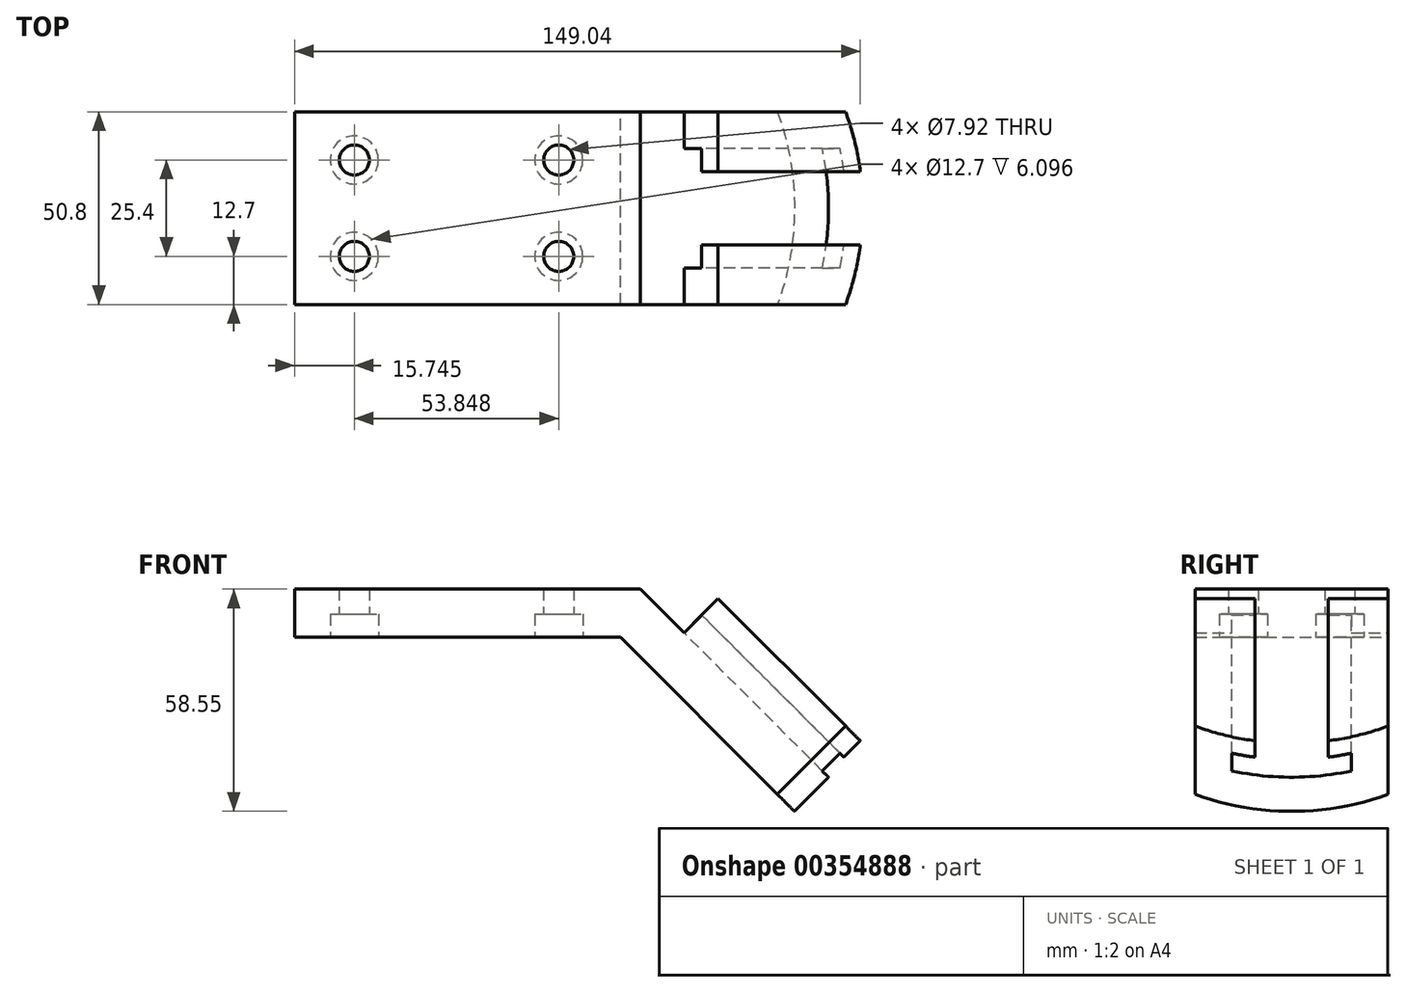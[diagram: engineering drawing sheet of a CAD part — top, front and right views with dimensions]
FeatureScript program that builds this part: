
annotation { "Feature Type Name" : "Feature", "Feature Type Description" : "" }
export const myFeature = defineFeature(function(context is Context, id is Id, definition is map)
    precondition{}
    {
        {
            var Q0;
            Q0=qCreatedBy(makeId("Front.planeOp"),FACE);
            var sketch = newSketch(context, id + "F0", { "sketchPlane" : qUnion([Q0])});
            skLineSegment(sketch, "E0.0.0", {"start": v(-91.11, -12.7) * mm, "end": v(-5.26, -12.7) * mm});
            skLineSegment(sketch, "E0.0.2", {"start": v(0, 0) * mm, "end": v(-91.11, 0) * mm});
            skLineSegment(sketch, "E0.0.3", {"start": v(-91.11, 0) * mm, "end": v(-91.11, -12.7) * mm});
            skLineSegment(sketch, "E1", {"start": v(0, 0) * mm, "end": v(49.57, -49.57) * mm});
            skLineSegment(sketch, "E2", {"start": v(49.57, -49.57) * mm, "end": v(40.6, -58.55) * mm});
            skLineSegment(sketch, "E3", {"start": v(40.6, -58.55) * mm, "end": v(-5.26, -12.7) * mm});
            skLineSegment(sketch, "E4", {"start": v(0, 0) * mm, "end": v(-18.71, 18.71) * mm, "construction": true});
            skLineSegment(sketch, "E5", {"start": v(49.57, -49.57) * mm, "end": v(58.55, -40.6) * mm});
            skLineSegment(sketch, "E6", {"start": v(58.55, -40.6) * mm, "end": v(20.47, -2.51) * mm});
            skLineSegment(sketch, "E7", {"start": v(20.47, -2.51) * mm, "end": v(11.5, -11.5) * mm});
            skSolve(sketch);
        }
        {
            var Q0;
            Q0=makeQuery(id+"F0.imprint","IMPRINT",FACE,{"disambiguationData":[TD([[makeQuery(id+"F0.imprint","IMPRINT",EDGE,{"derivedFrom":sQuery(id+"F0.wireOp",EDGE,"E0.0.0")}),1.0]])]});
            var Q1;
            {var subQ0=sQuery(id+"F0.wireOp",EDGE,"E5");Q1=makeQuery(id+"F0.imprint","IMPRINT",FACE,{"disambiguationData":[TD([[makeQuery(id+"F0.imprint","IMPRINT",EDGE,{"derivedFrom":subQ0}),1.0]])]});}
            extrude(context, id + "F1", {"entities" : qUnion([Q0, Q1]), "depth" : 50.8 * mm, "symmetric" : true});
        }
        {
            var Q0;
            Q0=makeQuery(id+"F1.opExtrude","SWEPT_FACE",FACE,{"disambiguationData":[OSD([sQuery(id+"F0.wireOp",EDGE,"E6")])]});
            var sketch = newSketch(context, id + "F2", { "sketchPlane" : qUnion([Q0])});
            skLineSegment(sketch, "E8.0.0", {"start": v(25.4, -70.1) * mm, "end": v(25.4, -16.26) * mm});
            skLineSegment(sketch, "E8.0.1", {"start": v(25.4, -16.26) * mm, "end": v(-25.4, -16.26) * mm});
            skLineSegment(sketch, "E8.0.2", {"start": v(-25.4, -16.26) * mm, "end": v(-25.4, -70.1) * mm});
            skLineSegment(sketch, "E8.0.3", {"start": v(-25.4, -70.1) * mm, "end": v(25.4, -70.1) * mm});
            skArc(sketch, "E9", {"start": v(-53.84, -17.33) * mm, "mid": v(0, -70.1) * mm, "end": v(53.84, -17.33) * mm});
            skLineSegment(sketch, "E10", {"start": v(0, 0) * mm, "end": v(0, -70.1) * mm, "construction": true});
            skSolve(sketch);
        }
        {
            var Q0;
            {var subQ0=sQuery(id+"F2.wireOp",EDGE,"E8.0.3");var subQ1=sQuery(id+"F2.wireOp",EDGE,"E8.0.0");var subQ2=makeQuery(id+"F2.imprint","INTERSECT",VERTEX,{"derivedFrom":[subQ1,subQ0]});Q0=makeQuery(id+"F2.imprint","IMPRINT",FACE,{"disambiguationData":[TD([[makeQuery(id+"F2.imprint","IMPRINT",EDGE,{"disambiguationData":[TD([[subQ2,-1.0]])],"derivedFrom":subQ1}),1.0]])]});}
            var Q1;
            {var subQ0=sQuery(id+"F2.wireOp",EDGE,"E8.0.3");var subQ1=sQuery(id+"F2.wireOp",EDGE,"E8.0.2");var subQ2=makeQuery(id+"F2.imprint","INTERSECT",VERTEX,{"derivedFrom":[subQ1,subQ0]});Q1=makeQuery(id+"F2.imprint","IMPRINT",FACE,{"disambiguationData":[TD([[makeQuery(id+"F2.imprint","IMPRINT",EDGE,{"disambiguationData":[TD([[subQ2,-1.0]])],"derivedFrom":subQ1}),-1.0]])]});}
            extrude(context, id + "F3", {"entities" : qUnion([Q0, Q1]), "operationType" : NewBodyOperationType.REMOVE, "endBound" : BoundingType.THROUGH_ALL, "oppositeDirection" : true, "depth" : 25.4 * mm});
        }
        {
            var Q0;
            Q0=makeQuery(id+"F1.opExtrude","SWEPT_FACE",FACE,{"disambiguationData":[OSD([sQuery(id+"F0.wireOp",EDGE,"E7")])]});
            var sketch = newSketch(context, id + "F4", { "sketchPlane" : qUnion([Q0])});
            skLineSegment(sketch, "E11.0.0", {"start": v(-25.4, 12.7) * mm, "end": v(-25.4, 0) * mm});
            skLineSegment(sketch, "E11.0.1", {"start": v(-25.4, 0) * mm, "end": v(25.4, 0) * mm});
            skLineSegment(sketch, "E11.0.2", {"start": v(25.4, 0) * mm, "end": v(25.4, 12.7) * mm});
            skLineSegment(sketch, "E11.0.3", {"start": v(25.4, 12.7) * mm, "end": v(-25.4, 12.7) * mm});
            skLineSegment(sketch, "E12", {"start": v(-9.65, 12.7) * mm, "end": v(-9.65, 6.6) * mm});
            skLineSegment(sketch, "E13", {"start": v(-9.65, 6.6) * mm, "end": v(-15.75, 6.6) * mm});
            skLineSegment(sketch, "E14", {"start": v(-15.75, 6.6) * mm, "end": v(-15.75, 0) * mm});
            skLineSegment(sketch, "E15", {"start": v(-15.75, 0) * mm, "end": v(15.75, 0) * mm});
            skLineSegment(sketch, "E16", {"start": v(15.75, 0) * mm, "end": v(15.75, 6.6) * mm});
            skLineSegment(sketch, "E17", {"start": v(15.75, 6.6) * mm, "end": v(9.65, 6.6) * mm});
            skLineSegment(sketch, "E18", {"start": v(9.65, 6.6) * mm, "end": v(9.65, 12.7) * mm});
            skLineSegment(sketch, "E19", {"start": v(9.65, 12.7) * mm, "end": v(-9.65, 12.7) * mm});
            skLineSegment(sketch, "E20", {"start": v(9.65, 12.7) * mm, "end": v(25.4, 12.7) * mm});
            skLineSegment(sketch, "E21", {"start": v(-9.65, 12.7) * mm, "end": v(-25.4, 12.7) * mm});
            skSolve(sketch);
        }
        {
            var Q0;
            Q0=makeQuery(id+"F4.imprint","IMPRINT",FACE,{"disambiguationData":[TD([[makeQuery(id+"F4.imprint","IMPRINT",EDGE,{"derivedFrom":sQuery(id+"F4.wireOp",EDGE,"E12")}),1.0]])]});
            extrude(context, id + "F5", {"entities" : qUnion([Q0]), "operationType" : NewBodyOperationType.REMOVE, "endBound" : BoundingType.THROUGH_ALL, "oppositeDirection" : true, "depth" : 25.4 * mm});
        }
        {
            var Q0;
            Q0=makeQuery(id+"F1.opExtrude","SWEPT_FACE",FACE,{"disambiguationData":[OSD([sQuery(id+"F0.wireOp",EDGE,"E0.0.2")])]});
            var sketch = newSketch(context, id + "F6", { "sketchPlane" : qUnion([Q0])});
            skCircle(sketch, "E22", {"center": v(-75.36, 12.7) * mm, "radius": 5.14 * mm});
            skCircle(sketch, "E23", {"center": v(-21.52, 12.7) * mm, "radius": 5.14 * mm});
            skCircle(sketch, "E24", {"center": v(-21.52, -12.7) * mm, "radius": 5.14 * mm});
            skCircle(sketch, "E25", {"center": v(-75.36, -12.7) * mm, "radius": 5.14 * mm});
            skLineSegment(sketch, "E26", {"start": v(-75.36, 12.7) * mm, "end": v(-21.52, 12.7) * mm, "construction": true});
            skLineSegment(sketch, "E27", {"start": v(-21.52, 12.7) * mm, "end": v(-21.52, -12.7) * mm, "construction": true});
            skLineSegment(sketch, "E28", {"start": v(-21.52, -12.7) * mm, "end": v(-75.36, -12.7) * mm, "construction": true});
            skLineSegment(sketch, "E29", {"start": v(-75.36, -12.7) * mm, "end": v(-75.36, 12.7) * mm, "construction": true});
            skSolve(sketch);
        }
        {
            var Q0;
            Q0=makeQuery(id+"F1.opExtrude","SWEPT_FACE",FACE,{"disambiguationData":[OSD([sQuery(id+"F0.wireOp",EDGE,"E0.0.0")])]});
            var sketch = newSketch(context, id + "F7", { "sketchPlane" : qUnion([Q0])});
            skPoint(sketch, "E30.0", {"position": v(-21.52, 12.7) * mm});
            skPoint(sketch, "E31.0", {"position": v(-75.36, 12.7) * mm});
            skPoint(sketch, "E32.0", {"position": v(-75.36, -12.7) * mm});
            skPoint(sketch, "E33.0", {"position": v(-21.52, -12.7) * mm});
            skSolve(sketch);
        }
        {
            var Q0;
            Q0=sQuery(id+"F7.wireOp",VERTEX,"E31.0");
            var Q1;
            Q1=sQuery(id+"F7.wireOp",VERTEX,"E30.0");
            var Q2;
            Q2=sQuery(id+"F7.wireOp",VERTEX,"E33.0");
            var Q3;
            Q3=sQuery(id+"F7.wireOp",VERTEX,"E32.0");
            var Q4;
            Q4=makeQuery(id+"F1.opExtrude","SWEPT_BODY",BODY,{"disambiguationData":[OSD([sQuery(id+"F0.wireOp",EDGE,"E0.0.0"),sQuery(id+"F0.wireOp",EDGE,"E0.0.2"),sQuery(id+"F0.wireOp",EDGE,"E0.0.3"),sQuery(id+"F0.wireOp",EDGE,"E1"),sQuery(id+"F0.wireOp",EDGE,"E2"),sQuery(id+"F0.wireOp",EDGE,"E3"),sQuery(id+"F0.wireOp",EDGE,"E5"),sQuery(id+"F0.wireOp",EDGE,"E6"),sQuery(id+"F0.wireOp",EDGE,"E7")])]});
            hole(context, id + "F8", {"style" : HoleStyle.C_BORE, "endStyle" : HoleEndStyle.THROUGH, "holeDiameter" : 7.92 * mm, "cBoreDiameter" : 12.7 * mm, "cBoreDepth" : 6.1 * mm, "isTappedThrough" : true, "tappedDepth" : 12.7 * mm, "tapClearance" : 3, "locations" : qUnion([Q0, Q1, Q2, Q3]), "scope" : qUnion([Q4])});
        }
    });
